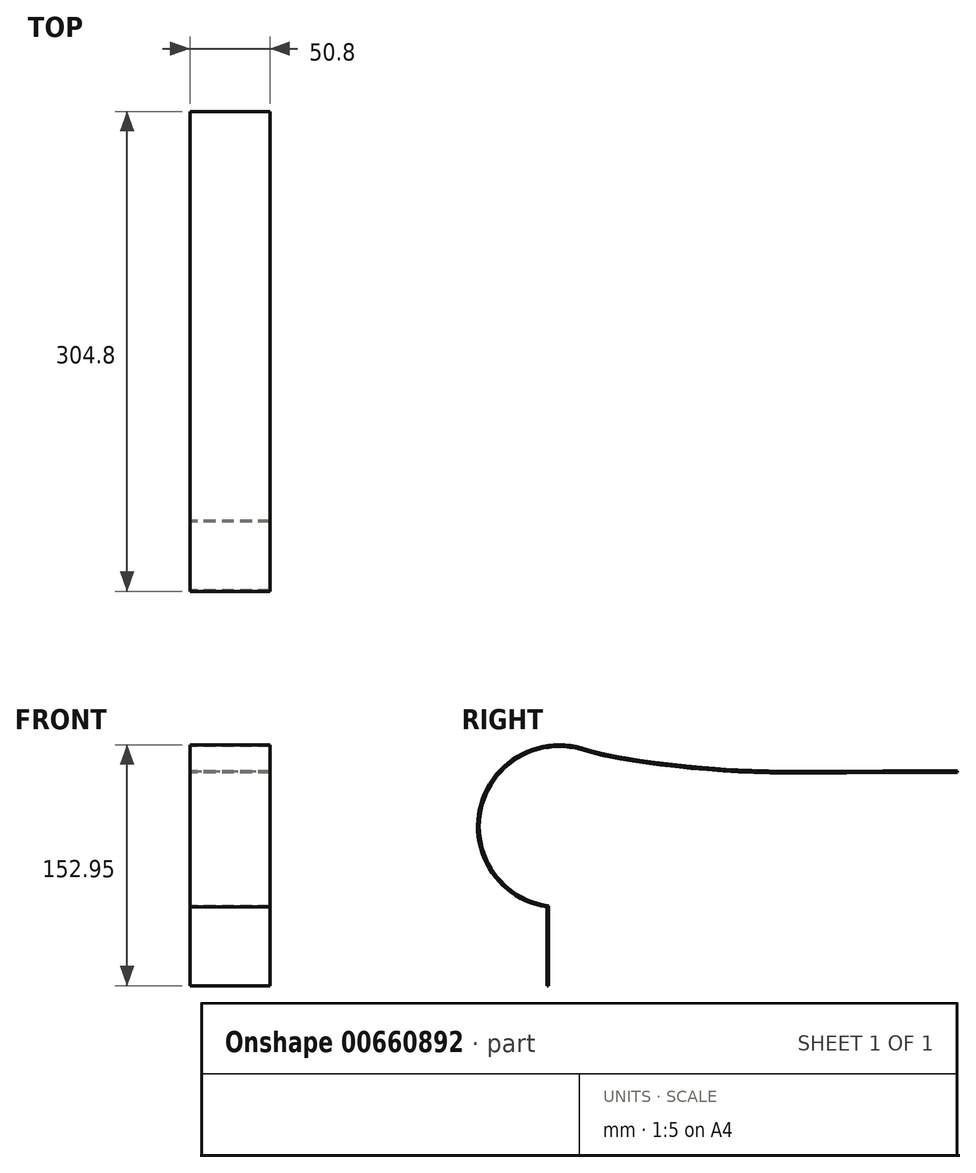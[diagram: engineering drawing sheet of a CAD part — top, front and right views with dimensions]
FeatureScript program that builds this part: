
annotation { "Feature Type Name" : "Feature", "Feature Type Description" : "" }
export const myFeature = defineFeature(function(context is Context, id is Id, definition is map)
    precondition{}
    {
        {
            var Q0;
            Q0=qCreatedBy(makeId("Right.planeOp"),FACE);
            var sketch = newSketch(context, id + "F0", { "sketchPlane" : qUnion([Q0])});
            skLineSegment(sketch, "E0", {"start": v(0, 0) * mm, "end": v(0, -50.8) * mm});
            skArc(sketch, "E1", {"start": v(20.68, 99.22) * mm, "mid": v(-42.87, 60.7) * mm, "end": v(0, 0) * mm});
            skFitSpline(sketch, "E2", {"points": [v(20.68, 99.22) * mm, v(40.2, 94.31) * mm, v(107.5, 85.9) * mm, v(259.85, 84.7) * mm], "startDerivative": vector(112.78, -31.93) * mm, "endDerivative": vector(496.64, 0) * mm});
            skLineSegment(sketch, "E3", {"start": v(-44.95, 94.31) * mm, "end": v(-44.95, 12.72) * mm, "construction": true});
            skLineSegment(sketch, "E4.0", {"start": v(-1.02, -0.88) * mm, "end": v(-1.02, -50.8) * mm});
            skArc(sketch, "E4.1", {"start": v(20.96, 100.2) * mm, "mid": v(-43.77, 61.34) * mm, "end": v(-1.02, -0.88) * mm});
            skFitSpline(sketch, "E4.2", {"points": [v(20.96, 100.2) * mm, v(23.3, 99.53) * mm, v(26.44, 98.63) * mm, v(30.55, 97.52) * mm, v(33.78, 96.72) * mm, v(36.76, 96.05) * mm, v(39.4, 95.5) * mm, v(41.55, 95.08) * mm, v(43.86, 94.65) * mm, v(47.13, 94.07) * mm, v(51.58, 93.33) * mm, v(57.4, 92.43) * mm, v(65.74, 91.24) * mm, v(77.02, 89.8) * mm, v(88.96, 88.5) * mm, v(98.63, 87.61) * mm, v(104.65, 87.12) * mm, v(109.42, 86.78) * mm, v(114.16, 86.47) * mm, v(120.06, 86.15) * mm, v(127.17, 85.84) * mm, v(136.8, 85.54) * mm, v(149.34, 85.33) * mm, v(165.82, 85.28) * mm, v(184.38, 85.37) * mm, v(212.78, 85.57) * mm, v(239.15, 85.72) * mm, v(259.85, 85.72) * mm]});
            skLineSegment(sketch, "E5", {"start": v(0, -50.8) * mm, "end": v(-1.02, -50.8) * mm});
            skLineSegment(sketch, "E6", {"start": v(259.85, 85.72) * mm, "end": v(259.85, 84.7) * mm});
            skPoint(sketch, "E7", {"position": v(-44.95, 50.33) * mm});
            skSolve(sketch);
        }
        {
            var Q0;
            Q0=makeQuery(id+"F0.imprint","IMPRINT",FACE,{"disambiguationData":[TD([[makeQuery(id+"F0.imprint","IMPRINT",EDGE,{"derivedFrom":sQuery(id+"F0.wireOp",EDGE,"E0")}),-1.0]])]});
            extrude(context, id + "F1", {"entities" : qUnion([Q0]), "depth" : 25.4 * mm, "offsetDistance" : 25.4 * mm, "hasSecondDirection" : true, "secondDirectionOppositeDirection" : true, "secondDirectionDepth" : 25.4 * mm});
        }
    });
